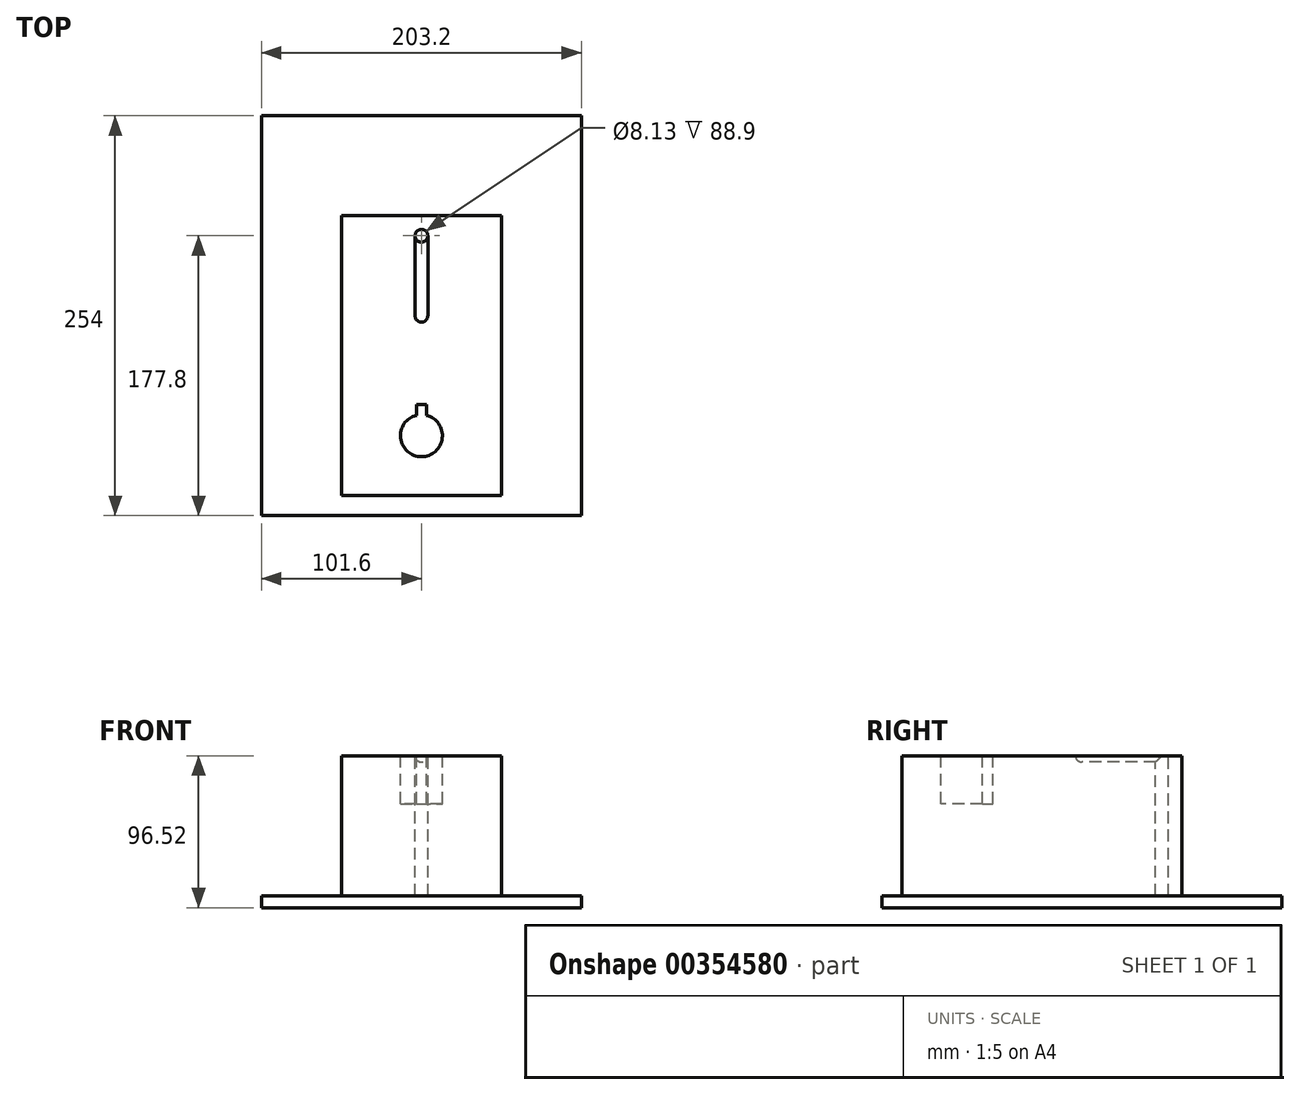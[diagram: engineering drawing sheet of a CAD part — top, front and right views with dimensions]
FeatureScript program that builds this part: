
annotation { "Feature Type Name" : "Feature", "Feature Type Description" : "" }
export const myFeature = defineFeature(function(context is Context, id is Id, definition is map)
    precondition{}
    {
        {
            var Q0;
            Q0=qCreatedBy(makeId("Top.planeOp"),FACE);
            var sketch = newSketch(context, id + "F0", { "sketchPlane" : qUnion([Q0])});
            skLineSegment(sketch, "E0.bottom", {"start": v(101.6, 101.6) * mm, "end": v(-101.6, 101.6) * mm});
            skLineSegment(sketch, "E0.top", {"start": v(101.6, -152.4) * mm, "end": v(-101.6, -152.4) * mm});
            skLineSegment(sketch, "E0.left", {"start": v(101.6, 101.6) * mm, "end": v(101.6, -152.4) * mm});
            skLineSegment(sketch, "E0.right", {"start": v(-101.6, 101.6) * mm, "end": v(-101.6, -152.4) * mm});
            skPoint(sketch, "E0.middle", {"position": v(0, -25.4) * mm});
            skSolve(sketch);
        }
        {
            var Q0;
            Q0=makeQuery(id+"F0.imprint","IMPRINT",FACE,{"disambiguationData":[TD([[makeQuery(id+"F0.imprint","IMPRINT",EDGE,{"derivedFrom":sQuery(id+"F0.wireOp",EDGE,"E0.bottom")}),1.0]])]});
            extrude(context, id + "F1", {"entities" : qUnion([Q0]), "depth" : 7.62 * mm});
        }
        {
            var Q0;
            Q0=makeQuery(id+"F1.opExtrude","CAP_FACE",FACE,{"disambiguationData":[OSD([sQuery(id+"F0.wireOp",EDGE,"E0.bottom"),sQuery(id+"F0.wireOp",EDGE,"E0.top"),sQuery(id+"F0.wireOp",EDGE,"E0.left"),sQuery(id+"F0.wireOp",EDGE,"E0.right")])],"isStart":false});
            var sketch = newSketch(context, id + "F2", { "sketchPlane" : qUnion([Q0])});
            skLineSegment(sketch, "E1.bottom", {"start": v(50.8, 38.1) * mm, "end": v(-50.8, 38.1) * mm});
            skLineSegment(sketch, "E1.top", {"start": v(50.8, -38.1) * mm, "end": v(-50.8, -38.1) * mm});
            skLineSegment(sketch, "E1.left", {"start": v(50.8, 38.1) * mm, "end": v(50.8, -38.1) * mm});
            skLineSegment(sketch, "E1.right", {"start": v(-50.8, 38.1) * mm, "end": v(-50.8, -38.1) * mm});
            skPoint(sketch, "E1.middle", {"position": v(0, 0) * mm});
            skSolve(sketch);
        }
        {
            var Q0;
            Q0=makeQuery(id+"F2.imprint","IMPRINT",FACE,{"disambiguationData":[TD([[makeQuery(id+"F2.imprint","IMPRINT",EDGE,{"derivedFrom":sQuery(id+"F2.wireOp",EDGE,"E1.bottom")}),1.0]])]});
            extrude(context, id + "F3", {"entities" : qUnion([Q0]), "operationType" : NewBodyOperationType.ADD, "depth" : 88.9 * mm});
        }
        {
            var Q0;
            Q0=makeQuery(id+"F3.opExtrude","CAP_FACE",FACE,{"disambiguationData":[OSD([sQuery(id+"F2.wireOp",EDGE,"E1.bottom"),sQuery(id+"F2.wireOp",EDGE,"E1.top"),sQuery(id+"F2.wireOp",EDGE,"E1.left"),sQuery(id+"F2.wireOp",EDGE,"E1.right")])],"isStart":false});
            var sketch = newSketch(context, id + "F4", { "sketchPlane" : qUnion([Q0])});
            skCircle(sketch, "E2", {"center": v(0, 25.4) * mm, "radius": 4.06 * mm});
            skSolve(sketch);
        }
        {
            var Q0;
            Q0=makeQuery(id+"F4.imprint","IMPRINT",FACE,{"disambiguationData":[TD([[makeQuery(id+"F4.imprint","IMPRINT",EDGE,{"derivedFrom":sQuery(id+"F4.wireOp",EDGE,"E2")}),1.0]])]});
            extrude(context, id + "F5", {"entities" : qUnion([Q0]), "operationType" : NewBodyOperationType.REMOVE, "oppositeDirection" : true, "depth" : 88.9 * mm});
        }
        {
            var Q0;
            Q0=makeQuery(id+"F3.opExtrude","CAP_FACE",FACE,{"disambiguationData":[OSD([sQuery(id+"F2.wireOp",EDGE,"E1.bottom"),sQuery(id+"F2.wireOp",EDGE,"E1.top"),sQuery(id+"F2.wireOp",EDGE,"E1.left"),sQuery(id+"F2.wireOp",EDGE,"E1.right")])],"isStart":false});
            var sketch = newSketch(context, id + "F6", { "sketchPlane" : qUnion([Q0])});
            skLineSegment(sketch, "E3.bottom", {"start": v(4.06, -25.4) * mm, "end": v(-4.06, -25.4) * mm, "construction": true});
            skLineSegment(sketch, "E3.top", {"start": v(4.06, 25.4) * mm, "end": v(-4.06, 25.4) * mm, "construction": true});
            skLineSegment(sketch, "E3.left", {"start": v(4.06, -25.4) * mm, "end": v(4.06, 25.4) * mm});
            skLineSegment(sketch, "E3.right", {"start": v(-4.06, -25.4) * mm, "end": v(-4.06, 25.4) * mm});
            skArc(sketch, "E4", {"start": v(-4.06, -25.4) * mm, "mid": v(0, -29.46) * mm, "end": v(4.06, -25.4) * mm});
            skArc(sketch, "E5", {"start": v(-4.06, 25.4) * mm, "mid": v(0, 29.46) * mm, "end": v(4.06, 25.4) * mm});
            skLineSegment(sketch, "E6", {"start": v(0, 29.46) * mm, "end": v(0, -29.46) * mm});
            skSolve(sketch);
        }
        {
            var Q0;
            {var subQ0=sQuery(id+"F6.wireOp",EDGE,"E3.left");Q0=makeQuery(id+"F6.imprint","IMPRINT",FACE,{"disambiguationData":[TD([[makeQuery(id+"F6.imprint","IMPRINT",EDGE,{"derivedFrom":subQ0}),1.0]])]});}
            var Q1;
            Q1=sQuery(id+"F6.wireOp",EDGE,"E6");
            revolve(context, id + "F7", {"operationType" : NewBodyOperationType.REMOVE, "entities" : qUnion([Q0]), "axis" : qUnion([Q1]), "revolveType" : RevolveType.FULL, "oppositeDirection" : true});
        }
        {
            var Q0;
            Q0=makeQuery(id+"F3.opExtrude","SWEPT_FACE",FACE,{"disambiguationData":[OSD([sQuery(id+"F2.wireOp",EDGE,"E1.top")])]});
            extrude(context, id + "F8", {"entities" : qUnion([Q0]), "operationType" : NewBodyOperationType.ADD, "depth" : 101.6 * mm});
        }
        {
            var Q0;
            {var subQ0=sQuery(id+"F2.wireOp",EDGE,"E1.top");Q0=makeQuery(id+"F8.boolean.opBoolean","MERGE",FACE,{"derivedFrom":[makeQuery(id+"F3.opExtrude","CAP_FACE",FACE,{"disambiguationData":[OSD([sQuery(id+"F2.wireOp",EDGE,"E1.bottom"),subQ0,sQuery(id+"F2.wireOp",EDGE,"E1.left"),sQuery(id+"F2.wireOp",EDGE,"E1.right")])],"isStart":false}),makeQuery(id+"F8.opExtrude","SWEPT_FACE",FACE,{"disambiguationData":[OSD([subQ0]),TDD([makeQuery(id+"F3.opExtrude","CAP_EDGE",EDGE,{"disambiguationData":[OSD([subQ0])],"isStart":false})])]})]});}
            var sketch = newSketch(context, id + "F9", { "sketchPlane" : qUnion([Q0])});
            skArc(sketch, "E7", {"start": v(-3.17, -88.65) * mm, "mid": v(0, -114.94) * mm, "end": v(3.18, -88.65) * mm});
            skLineSegment(sketch, "E8.top", {"start": v(-3.17, -81.91) * mm, "end": v(3.17, -81.91) * mm});
            skLineSegment(sketch, "E8.left", {"start": v(-3.18, -88.65) * mm, "end": v(-3.17, -81.91) * mm});
            skLineSegment(sketch, "E8.right", {"start": v(3.17, -88.65) * mm, "end": v(3.18, -81.91) * mm});
            skPoint(sketch, "E9.orphan", {"position": v(3.18, -101.6) * mm});
            skPoint(sketch, "E8.bottom.start.orphan", {"position": v(-3.18, -101.6) * mm});
            skSolve(sketch);
        }
        {
            var Q0;
            Q0=makeQuery(id+"F9.imprint","IMPRINT",FACE,{"disambiguationData":[TD([[makeQuery(id+"F9.imprint","IMPRINT",EDGE,{"derivedFrom":sQuery(id+"F9.wireOp",EDGE,"E7")}),1.0]])]});
            extrude(context, id + "F10", {"entities" : qUnion([Q0]), "operationType" : NewBodyOperationType.REMOVE, "oppositeDirection" : true, "depth" : 30.48 * mm});
        }
    });
